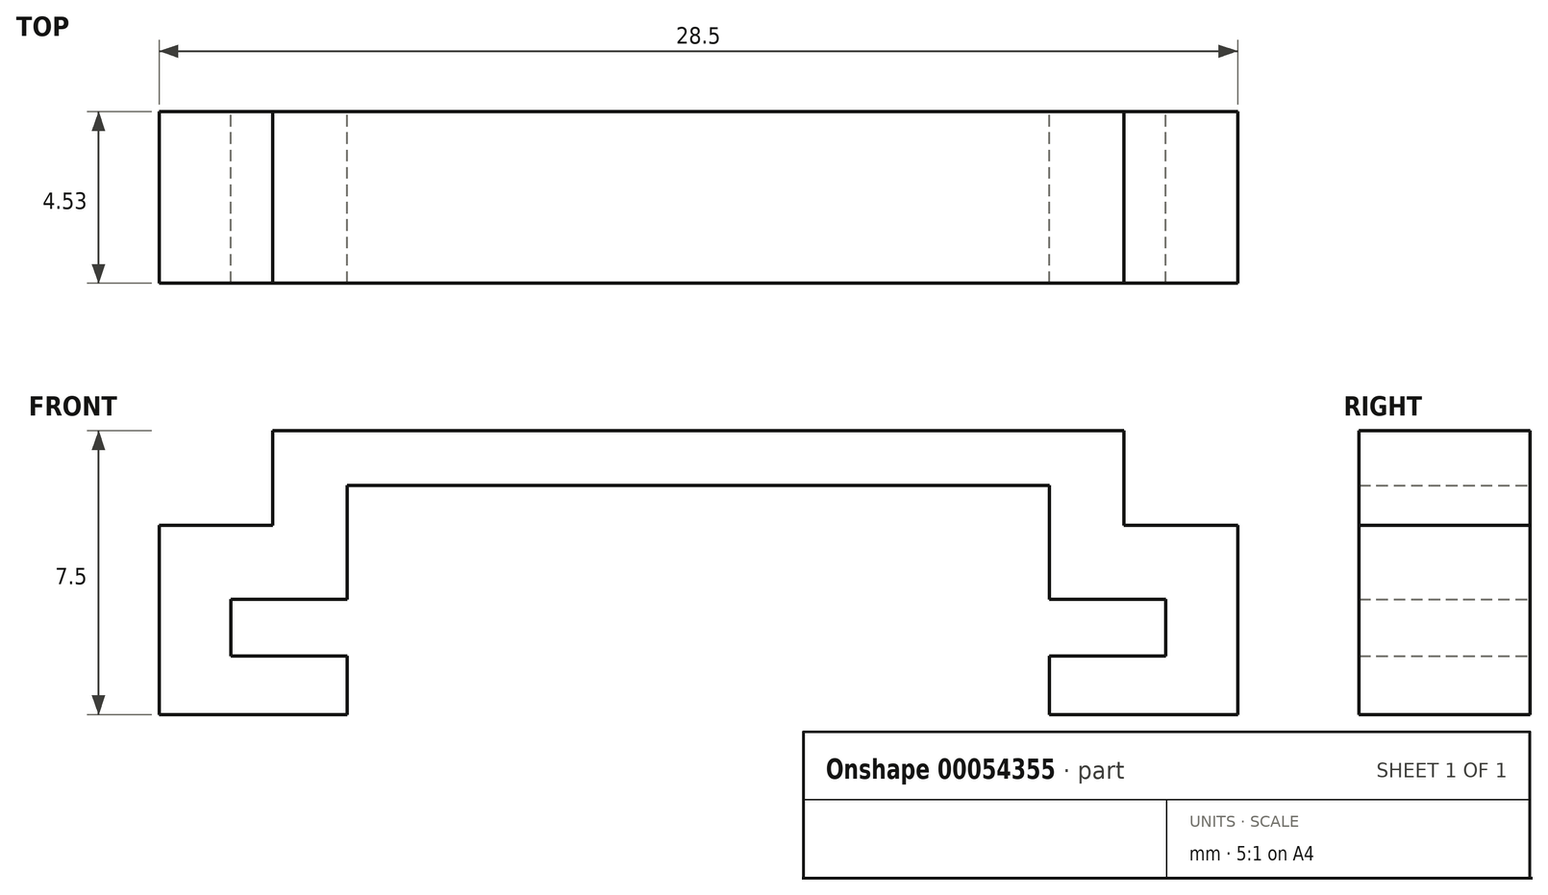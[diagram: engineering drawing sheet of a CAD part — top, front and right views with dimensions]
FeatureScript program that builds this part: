
annotation { "Feature Type Name" : "Feature", "Feature Type Description" : "" }
export const myFeature = defineFeature(function(context is Context, id is Id, definition is map)
    precondition{}
    {
        {
            var Q0;
            Q0=qCreatedBy(makeId("Front.planeOp"),FACE);
            var sketch = newSketch(context, id + "F0", { "sketchPlane" : qUnion([Q0])});
            skLineSegment(sketch, "E0", {"start": v(0, 0) * mm, "end": v(-16.25, 0) * mm});
            skLineSegment(sketch, "E1", {"start": v(0, 0) * mm, "end": v(16.25, 0) * mm});
            skLineSegment(sketch, "E2", {"start": v(16.25, 0) * mm, "end": v(16.25, 1.5) * mm});
            skLineSegment(sketch, "E3", {"start": v(-16.25, 0) * mm, "end": v(-16.25, 1.5) * mm});
            skLineSegment(sketch, "E4", {"start": v(-16.25, 1.5) * mm, "end": v(-9.28, 1.5) * mm});
            skLineSegment(sketch, "E5", {"start": v(16.25, 1.5) * mm, "end": v(9.28, 1.5) * mm});
            skLineSegment(sketch, "E6", {"start": v(-9.28, 1.5) * mm, "end": v(-9.28, 3.05) * mm});
            skLineSegment(sketch, "E7", {"start": v(9.28, 1.5) * mm, "end": v(9.28, 3.05) * mm});
            skLineSegment(sketch, "E8", {"start": v(-9.28, 3.05) * mm, "end": v(-12.35, 3.05) * mm});
            skLineSegment(sketch, "E9", {"start": v(9.28, 3.05) * mm, "end": v(12.35, 3.05) * mm});
            skLineSegment(sketch, "E10", {"start": v(-12.35, 3.05) * mm, "end": v(-12.35, 4.55) * mm});
            skLineSegment(sketch, "E11", {"start": v(12.35, 3.05) * mm, "end": v(12.35, 4.55) * mm});
            skLineSegment(sketch, "E12", {"start": v(-12.35, 4.55) * mm, "end": v(-9.28, 4.55) * mm});
            skLineSegment(sketch, "E13", {"start": v(12.35, 4.55) * mm, "end": v(9.28, 4.55) * mm});
            skLineSegment(sketch, "E14", {"start": v(-9.28, 4.55) * mm, "end": v(-9.28, 7.55) * mm});
            skLineSegment(sketch, "E15", {"start": v(9.28, 4.55) * mm, "end": v(9.28, 7.55) * mm});
            skLineSegment(sketch, "E16", {"start": v(9.28, 7.55) * mm, "end": v(-9.28, 7.55) * mm});
            skLineSegment(sketch, "E17", {"start": v(-16.25, 1.5) * mm, "end": v(-14.25, 1.5) * mm});
            skPoint(sketch, "E17.endSnap0", {"position": v(-12.76, 1.5) * mm});
            skLineSegment(sketch, "E18", {"start": v(16.25, 1.5) * mm, "end": v(14.25, 1.5) * mm});
            skLineSegment(sketch, "E19", {"start": v(14.25, 1.5) * mm, "end": v(14.25, 6.5) * mm});
            skLineSegment(sketch, "E20", {"start": v(-14.25, 1.5) * mm, "end": v(-14.25, 6.5) * mm});
            skLineSegment(sketch, "E21", {"start": v(-14.25, 6.5) * mm, "end": v(-11.25, 6.5) * mm});
            skLineSegment(sketch, "E22", {"start": v(14.25, 6.5) * mm, "end": v(11.25, 6.5) * mm});
            skLineSegment(sketch, "E23", {"start": v(11.25, 6.5) * mm, "end": v(11.25, 9) * mm});
            skLineSegment(sketch, "E24", {"start": v(-11.25, 6.5) * mm, "end": v(-11.25, 9) * mm});
            skLineSegment(sketch, "E25", {"start": v(-11.25, 9) * mm, "end": v(11.25, 9) * mm});
            skSolve(sketch);
        }
        {
            var Q0;
            Q0=makeQuery(id+"F0.imprint","IMPRINT",FACE,{"disambiguationData":[TD([[makeQuery(id+"F0.imprint","IMPRINT",EDGE,{"derivedFrom":sQuery(id+"F0.wireOp",EDGE,"E4")}),1.0]])]});
            extrude(context, id + "F1", {"entities" : qUnion([Q0]), "depth" : 4.53 * mm});
        }
    });
